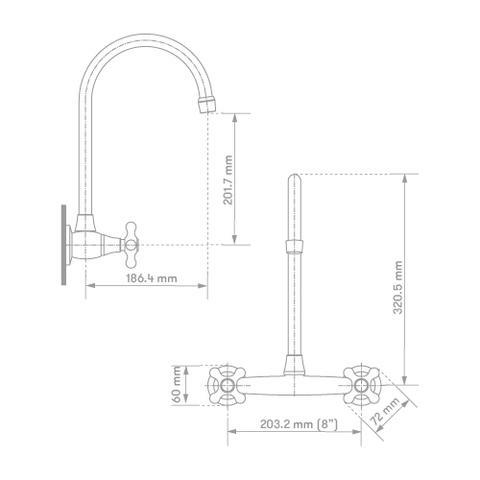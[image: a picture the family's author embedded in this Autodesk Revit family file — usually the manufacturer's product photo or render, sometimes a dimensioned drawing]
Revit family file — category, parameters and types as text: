
# Revit family: 01-2832-11-MEZCLADOR PARED 8” METAL PRISTINA
name_source: partatom
category: Plumbing Fixtures
revit_build: Autodesk Revit 2018 (Build: 20170223_1515(x64)
units: mm (PartAtom-declared; Revit-internal decimal feet)

## family parameters
Cut with Voids When Loaded = No
Host = Face
OmniClass Number = 23.31.11.00
Part Type = Normal
Room Calculation Point = No
Round Connector Dimension = Use Diameter
Shared = No

## types (1)
- 01-2832-11
    Alto = 320.5 mm  [stored 1.05151 ft]
    Alto - aireador = 201.7 mm
    Ancho manija = 75 mm
    CW Connection = Yes
    Default Elevation = 0 mm  [stored 0 ft]
    Description = Bimando
    Eje - (roscas) = 203.2 mm  [stored 0.666667 ft]
    Eje-Aireador = 186.4 mm
    Escudo = 65 mm
    HW Connection = Yes
    Link Ficha Tecnica = http://infotecnica.gricol.com
    Manufacturer = Gricol
    Metal Laton Cromado = Metal Laton Cromado
    Metal Zamak Cromado = Metal Zamak Cromado
    Model = 01-2832-11
    Plastico - ABS Cromado = Plastico - ABS Cromado
    Product Name = MEZCLADOR PARED 8” METAL PRISTINA
    Type Image = MEZCLADOR PARED PRISTINA.jpg
    URL = https://www.gricol.com
    Vent Connection = No
    Waste Connection = No

note: [stored X ft] marks values corroborated as IEEE doubles in the binary element streams (Revit-internal decimal feet)

## geometry (parser evidence)
native form markers: Blend x2, Sweep x4
no freeform markers — native parametric forms only
